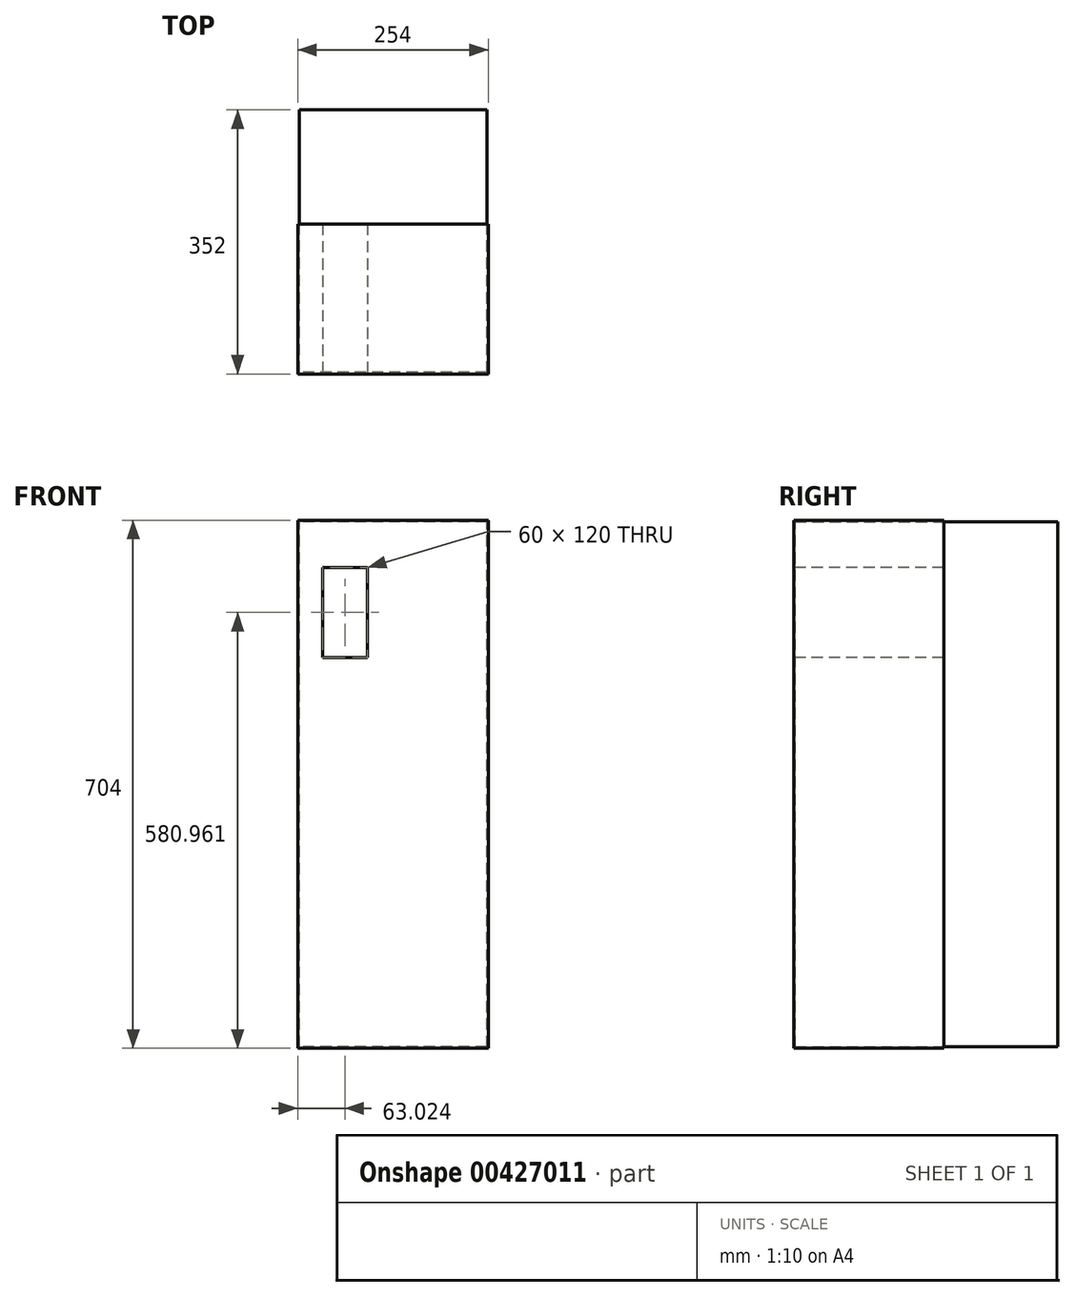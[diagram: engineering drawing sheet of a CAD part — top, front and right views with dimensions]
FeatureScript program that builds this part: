
annotation { "Feature Type Name" : "Feature", "Feature Type Description" : "" }
export const myFeature = defineFeature(function(context is Context, id is Id, definition is map)
    precondition{}
    {
        {
            var Q0;
            Q0=qCreatedBy(makeId("Front.planeOp"),FACE);
            var sketch = newSketch(context, id + "F0", { "sketchPlane" : qUnion([Q0])});
            skLineSegment(sketch, "E0.bottom", {"start": v(0, 0) * mm, "end": v(-250, 0) * mm});
            skLineSegment(sketch, "E0.top", {"start": v(0, 700) * mm, "end": v(-250, 700) * mm});
            skLineSegment(sketch, "E0.left", {"start": v(0, 0) * mm, "end": v(0, 700) * mm});
            skLineSegment(sketch, "E0.right", {"start": v(-250, 0) * mm, "end": v(-250, 700) * mm});
            skSolve(sketch);
        }
        {
            var Q0;
            Q0=makeQuery(id+"F0.imprint","IMPRINT",FACE,{"disambiguationData":[TD([[makeQuery(id+"F0.imprint","IMPRINT",EDGE,{"derivedFrom":sQuery(id+"F0.wireOp",EDGE,"E0.bottom")}),-1.0]])]});
            extrude(context, id + "F1", {"entities" : qUnion([Q0]), "endBound" : BoundingType.SYMMETRIC, "depth" : 350 * mm});
        }
        {
            var Q0;
            Q0=makeQuery(id+"F1.opExtrude","CAP_FACE",FACE,{"disambiguationData":[OSD([sQuery(id+"F0.wireOp",EDGE,"E0.bottom"),sQuery(id+"F0.wireOp",EDGE,"E0.top"),sQuery(id+"F0.wireOp",EDGE,"E0.left"),sQuery(id+"F0.wireOp",EDGE,"E0.right")])],"isStart":false});
            cPlane(context, id + "F2", {"entities" : qUnion([Q0]), "cplaneType" : CPlaneType.OFFSET, "offset" : 2 * mm, "width" : 150 * mm, "height" : 150 * mm});
        }
        {
            var Q0;
            Q0=qCreatedBy(id+"F2.planeOp",FACE);
            var sketch = newSketch(context, id + "F3", { "sketchPlane" : qUnion([Q0])});
            skLineSegment(sketch, "E1.bottom", {"start": v(-252, 702) * mm, "end": v(2, 702) * mm});
            skLineSegment(sketch, "E1.top", {"start": v(-252, -2) * mm, "end": v(2, -2) * mm});
            skLineSegment(sketch, "E1.left", {"start": v(-252, 702) * mm, "end": v(-252, -2) * mm});
            skLineSegment(sketch, "E1.right", {"start": v(2, 702) * mm, "end": v(2, -2) * mm});
            skLineSegment(sketch, "E2.0.0", {"start": v(0, 0) * mm, "end": v(0, 700) * mm});
            skLineSegment(sketch, "E2.0.1", {"start": v(0, 700) * mm, "end": v(-250, 700) * mm});
            skLineSegment(sketch, "E2.0.2", {"start": v(-250, 700) * mm, "end": v(-250, 0) * mm});
            skLineSegment(sketch, "E2.0.3", {"start": v(-250, 0) * mm, "end": v(0, 0) * mm});
            skLineSegment(sketch, "E3.bottom", {"start": v(-218.98, 638.96) * mm, "end": v(-158.98, 638.96) * mm});
            skLineSegment(sketch, "E3.top", {"start": v(-218.98, 518.96) * mm, "end": v(-158.98, 518.96) * mm});
            skLineSegment(sketch, "E3.left", {"start": v(-218.98, 638.96) * mm, "end": v(-218.98, 518.96) * mm});
            skLineSegment(sketch, "E3.right", {"start": v(-158.98, 638.96) * mm, "end": v(-158.98, 518.96) * mm});
            skSolve(sketch);
        }
        {
            var Q0;
            Q0=makeQuery(id+"F3.imprint","IMPRINT",FACE,{"disambiguationData":[TD([[makeQuery(id+"F3.imprint","IMPRINT",EDGE,{"derivedFrom":sQuery(id+"F3.wireOp",EDGE,"E2.0.0")}),1.0]])]});
            var Q1;
            Q1=makeQuery(id+"F3.imprint","IMPRINT",FACE,{"disambiguationData":[TD([[makeQuery(id+"F3.imprint","IMPRINT",EDGE,{"derivedFrom":sQuery(id+"F3.wireOp",EDGE,"E1.bottom")}),-1.0]])]});
            extrude(context, id + "F4", {"entities" : qUnion([Q0, Q1]), "oppositeDirection" : true, "depth" : 200 * mm});
        }
    });
